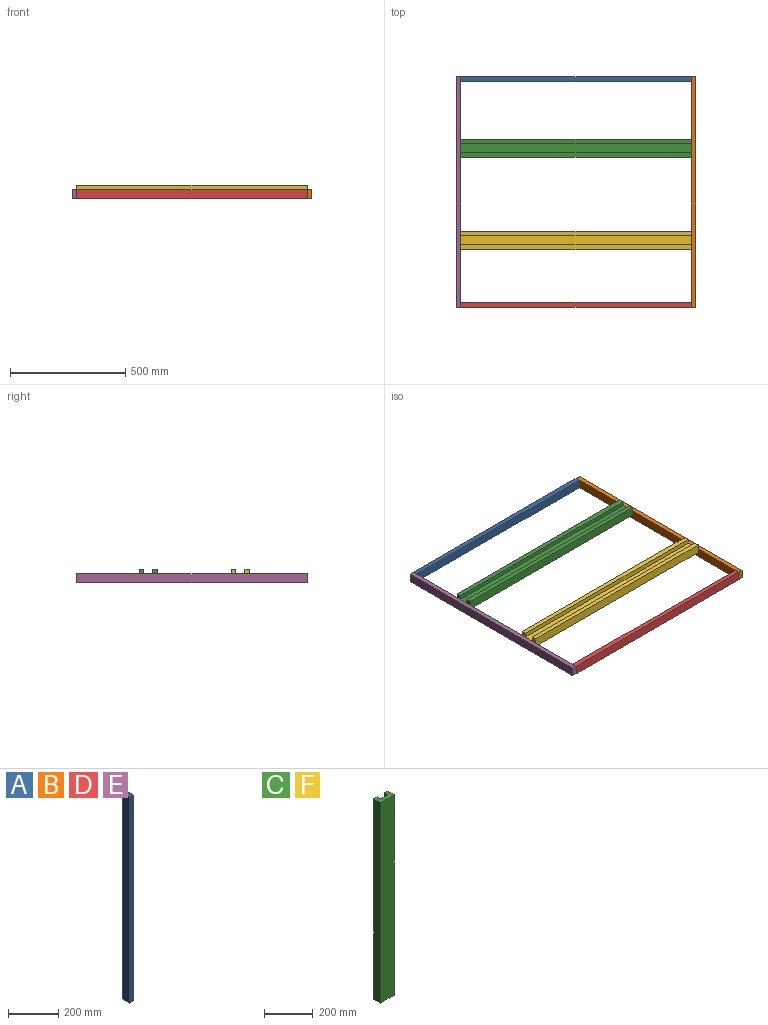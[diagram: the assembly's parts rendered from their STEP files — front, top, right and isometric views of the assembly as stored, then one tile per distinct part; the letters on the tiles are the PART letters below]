
ASSEMBLY  parts=6 mates=2
PART A: 6 faces, bbox 20x40x1000 mm
  f0: plane 1000x40mm, normal (1,0,0), area 40000mm2, adj f1,f3,f4,f5
  f1: plane 1000x20mm, normal (0,1,0), area 20000mm2, adj f0,f2,f4,f5
  f2: plane 1000x40mm, normal (-1,0,0), area 40000mm2, adj f1,f3,f4,f5
  f3: plane 1000x20mm, normal (0,-1,0), area 20000mm2, adj f0,f2,f4,f5
  f4: plane 40x20mm, normal (0,0,1), area 800mm2, adj f0,f1,f2,f3
  f5: plane 40x20mm, normal (0,0,-1), area 800mm2, adj f0,f1,f2,f3
PART B: same geometry as A
PART C: 10 faces, bbox 80x40x1000 mm
  f0: plane 1000x20mm, normal (0,1,0), area 20000mm2, adj f1,f7,f8,f9
  f1: plane 1000x40mm, normal (-1,0,0), area 40000mm2, adj f0,f2,f8,f9
  f2: plane 1000x80mm, normal (0,-1,0), area 80000mm2, adj f1,f3,f8,f9
  f3: plane 1000x40mm, normal (1,0,0), area 40000mm2, adj f2,f4,f8,f9
  f4: plane 1000x20mm, normal (0,1,0), area 20000mm2, adj f3,f5,f8,f9
  f5: plane 1000x20mm, normal (-1,0,0), area 20000mm2, adj f4,f6,f8,f9
  f6: plane 1000x40mm, normal (0,1,0), area 40000mm2, adj f5,f7,f8,f9
  f7: plane 1000x20mm, normal (1,0,0), area 20000mm2, adj f0,f6,f8,f9
  f8: plane 80x40mm, normal (0,0,1), area 2400mm2, adj f0,f1,f2,f3,f4,f5,f6,f7
  f9: plane 80x40mm, normal (0,0,-1), area 2400mm2, adj f0,f1,f2,f3,f4,f5,f6,f7
PART D: same geometry as A
PART E: same geometry as A
PART F: same geometry as C
PLACE A rot(axis=(-0.58,0.58,-0.58),120deg) t=(0,990,20)mm
PLACE B rot(axis=(-1,0,0),90deg) t=(1010,0,20)mm
PLACE C rot(axis=(0.58,-0.58,-0.58),120deg) t=(1000,760,40)mm
PLACE D rot(axis=(-0.58,0.58,-0.58),120deg) t=(0,10,20)mm
PLACE E rot(axis=(-1,0,0),90deg) t=(-10,0,20)mm
PLACE F rot(axis=(0.58,-0.58,-0.58),120deg) t=(1000,360,40)mm
MATE fastened D.f5 <-> E.f0  axis (-1,0,0) through (0,0,0)mm
MATE fastened F.f8 <-> E.f0  axis (-1,0,0) through (0,250,20)mm
